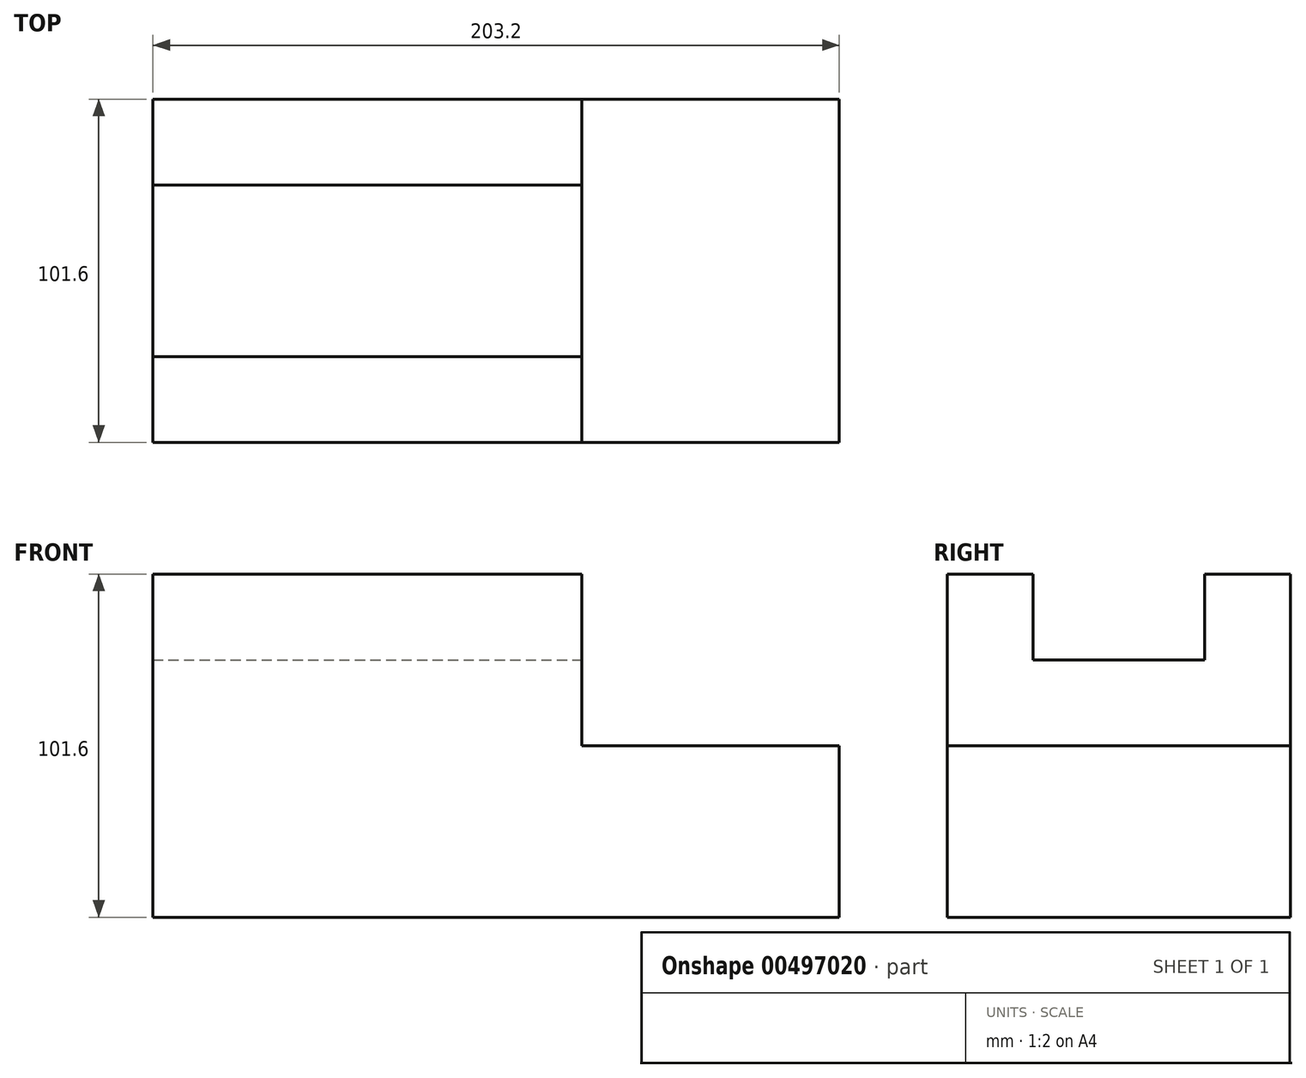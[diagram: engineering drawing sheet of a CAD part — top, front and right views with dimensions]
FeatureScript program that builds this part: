
annotation { "Feature Type Name" : "Feature", "Feature Type Description" : "" }
export const myFeature = defineFeature(function(context is Context, id is Id, definition is map)
    precondition{}
    {
        {
            var Q0;
            Q0=qCreatedBy(makeId("Front.planeOp"),FACE);
            var sketch = newSketch(context, id + "F0", { "sketchPlane" : qUnion([Q0])});
            skLineSegment(sketch, "E0.bottom", {"start": v(0, 0) * mm, "end": v(203.2, 0) * mm});
            skLineSegment(sketch, "E0.top", {"start": v(0, 101.6) * mm, "end": v(127, 101.6) * mm});
            skLineSegment(sketch, "E0.left", {"start": v(0, 0) * mm, "end": v(0, 101.6) * mm});
            skLineSegment(sketch, "E0.right", {"start": v(203.2, 0) * mm, "end": v(203.2, 50.8) * mm});
            skLineSegment(sketch, "E1", {"start": v(203.2, 50.8) * mm, "end": v(127, 50.8) * mm});
            skPoint(sketch, "E1.endSnap0", {"position": v(203.2, 50.8) * mm});
            skLineSegment(sketch, "E2", {"start": v(127, 50.8) * mm, "end": v(127, 101.6) * mm});
            skPoint(sketch, "E3.orphan", {"position": v(203.2, 101.6) * mm});
            skSolve(sketch);
        }
        {
            var Q0;
            Q0=makeQuery(id+"F0.imprint","IMPRINT",FACE,{"disambiguationData":[TD([[makeQuery(id+"F0.imprint","IMPRINT",EDGE,{"derivedFrom":sQuery(id+"F0.wireOp",EDGE,"E0.bottom")}),1.0]])]});
            extrude(context, id + "F1", {"entities" : qUnion([Q0]), "oppositeDirection" : true, "depth" : 101.6 * mm});
        }
        {
            var Q0;
            Q0=makeQuery(id+"F1.opExtrude","SWEPT_FACE",FACE,{"disambiguationData":[OSD([sQuery(id+"F0.wireOp",EDGE,"E0.top")])]});
            var sketch = newSketch(context, id + "F2", { "sketchPlane" : qUnion([Q0])});
            skLineSegment(sketch, "E4", {"start": v(0, 0) * mm, "end": v(0, 25.4) * mm});
            skLineSegment(sketch, "E5", {"start": v(0, 101.6) * mm, "end": v(0, 76.2) * mm});
            skLineSegment(sketch, "E6", {"start": v(0, 25.4) * mm, "end": v(127, 25.4) * mm});
            skLineSegment(sketch, "E7", {"start": v(0, 76.2) * mm, "end": v(127, 76.2) * mm});
            skLineSegment(sketch, "E8", {"start": v(0, 76.2) * mm, "end": v(0, 25.4) * mm});
            skSolve(sketch);
        }
        {
            var Q0;
            {var subQ0=sQuery(id+"F2.wireOp",EDGE,"E6");Q0=makeQuery(id+"F2.imprint","IMPRINT",FACE,{"disambiguationData":[TD([[makeQuery(id+"F2.imprint","IMPRINT",EDGE,{"derivedFrom":subQ0}),1.0]])]});}
            extrude(context, id + "F3", {"entities" : qUnion([Q0]), "operationType" : NewBodyOperationType.REMOVE, "oppositeDirection" : true, "depth" : 25.4 * mm});
        }
    });
